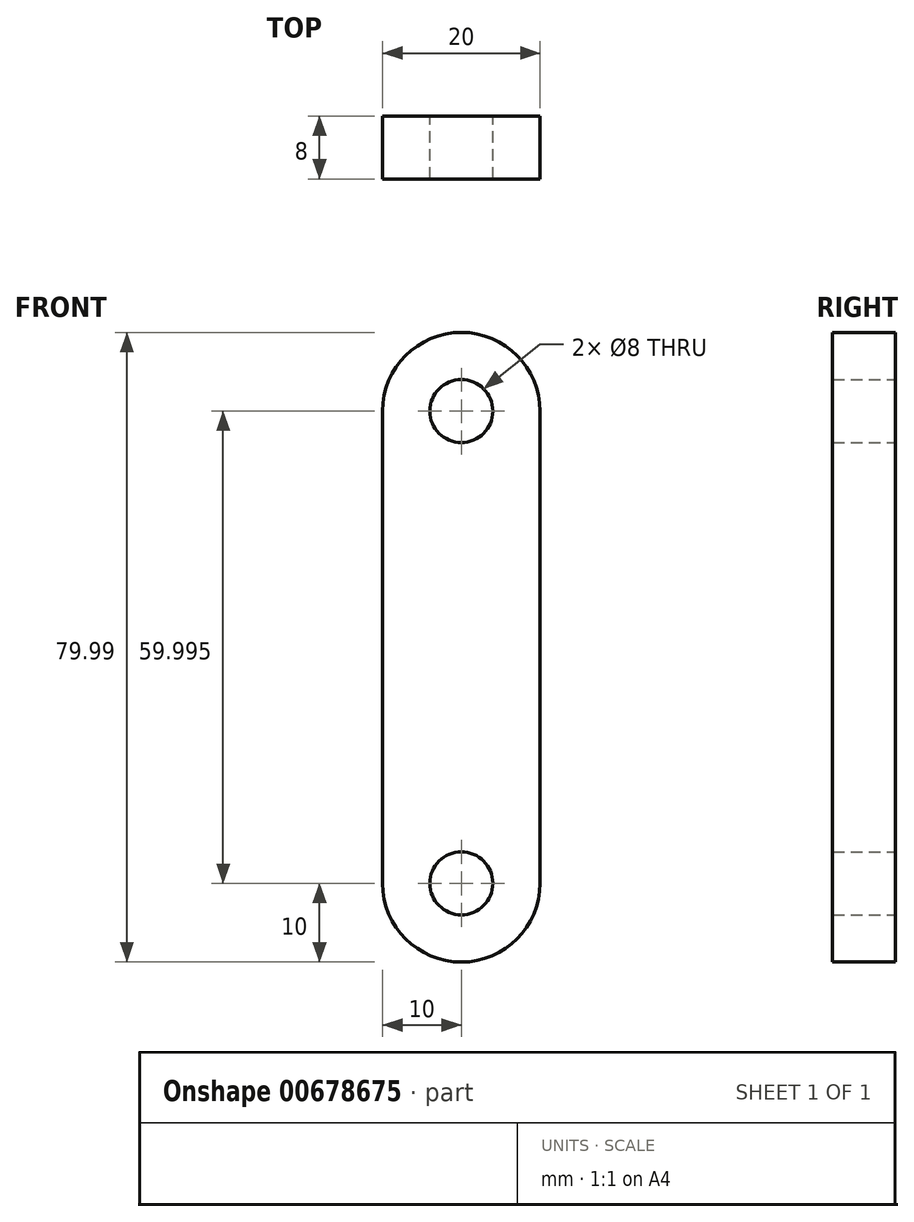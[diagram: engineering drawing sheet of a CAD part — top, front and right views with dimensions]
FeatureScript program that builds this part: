
annotation { "Feature Type Name" : "Feature", "Feature Type Description" : "" }
export const myFeature = defineFeature(function(context is Context, id is Id, definition is map)
    precondition{}
    {
        {
            var Q0;
            Q0=qCreatedBy(makeId("Front.planeOp"),FACE);
            var sketch = newSketch(context, id + "F0", { "sketchPlane" : qUnion([Q0])});
            skArc(sketch, "E0", {"start": v(10, 60) * mm, "mid": v(0, 70) * mm, "end": v(-10, 60) * mm});
            skCircle(sketch, "E1", {"center": v(0, 60) * mm, "radius": 4 * mm});
            skArc(sketch, "E2", {"start": v(-10, 0) * mm, "mid": v(0, -10) * mm, "end": v(10, 0) * mm});
            skCircle(sketch, "E3", {"center": v(0, 0) * mm, "radius": 4 * mm});
            skLineSegment(sketch, "E4", {"start": v(10, 60) * mm, "end": v(10, 0) * mm});
            skLineSegment(sketch, "E5", {"start": v(-10, 0) * mm, "end": v(-10, 60) * mm});
            skSolve(sketch);
        }
        {
            var Q0;
            Q0 = qSketchRegion(id + "F0", true);
            extrude(context, id + "F1", {"entities" : qUnion([Q0]), "depth" : 8 * mm, "offsetDistance" : 25.4 * mm});
        }
    });
